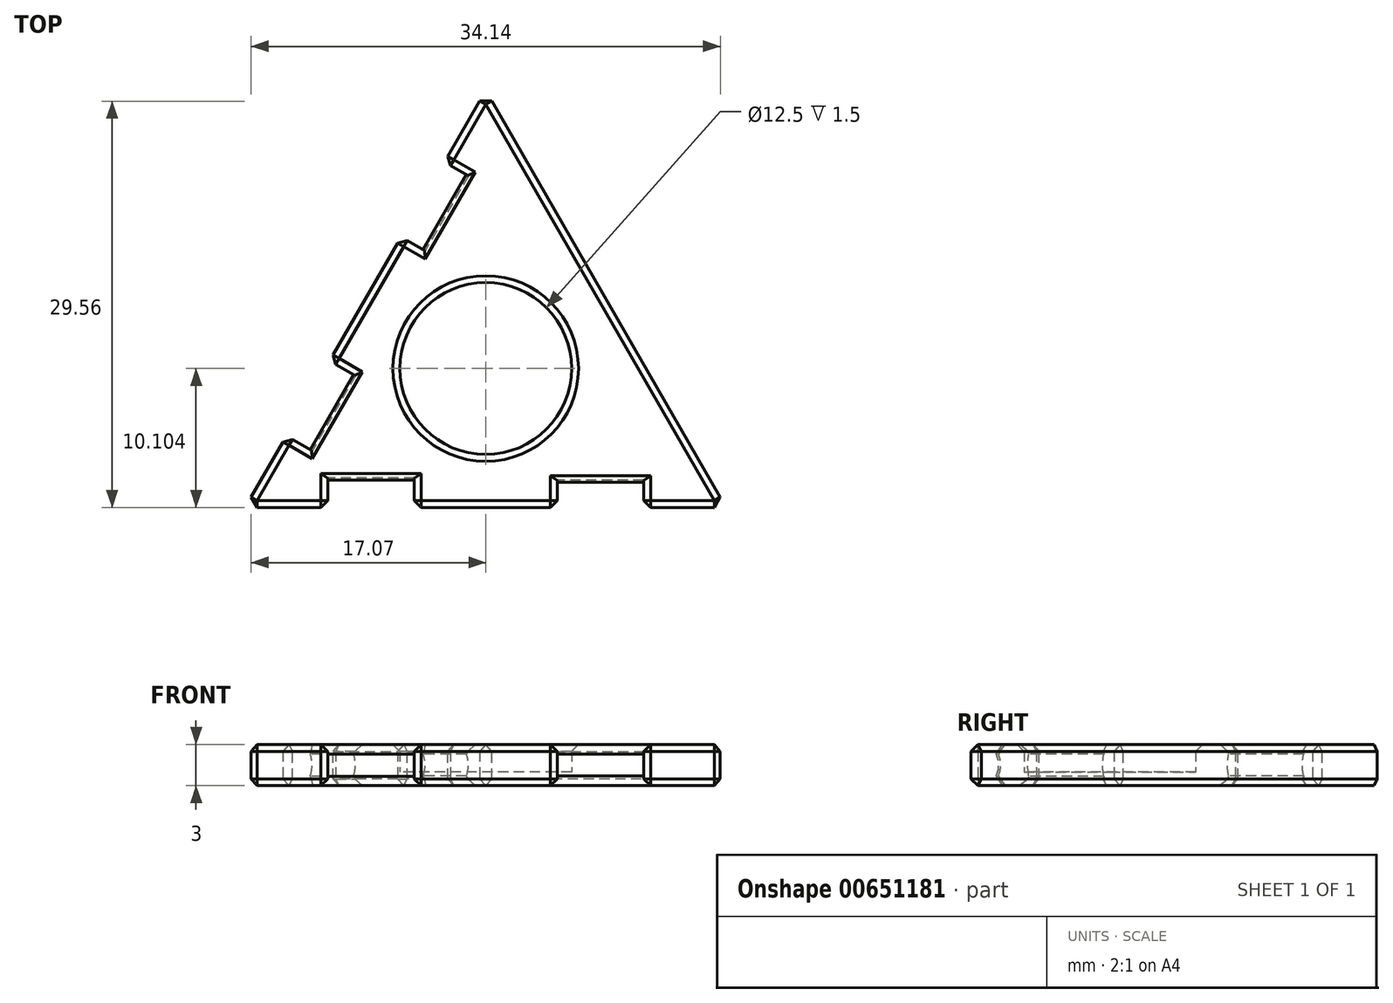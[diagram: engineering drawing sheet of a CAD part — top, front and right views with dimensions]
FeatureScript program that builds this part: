
annotation { "Feature Type Name" : "Feature", "Feature Type Description" : "" }
export const myFeature = defineFeature(function(context is Context, id is Id, definition is map)
    precondition{}
    {
        {
            var Q0;
            Q0=qCreatedBy(makeId("Top.planeOp"),FACE);
            cPlane(context, id + "F0", {"entities" : qUnion([Q0]), "cplaneType" : CPlaneType.OFFSET, "offset" : 1.5 * mm, "oppositeDirection" : true, "width" : 150 * mm, "height" : 150 * mm});
        }
        {
            var Q0;
            Q0=qCreatedBy(id+"F0.planeOp",FACE);
            var sketch = newSketch(context, id + "F1", { "sketchPlane" : qUnion([Q0])});
            skLineSegment(sketch, "E0", {"start": v(-17.5, 0) * mm, "end": v(0, 30.31) * mm});
            skLineSegment(sketch, "E1", {"start": v(0, 30.31) * mm, "end": v(17.5, 0) * mm});
            skLineSegment(sketch, "E2", {"start": v(17.5, 0) * mm, "end": v(-17.5, 0) * mm});
            skLineSegment(sketch, "E3", {"start": v(0, 0) * mm, "end": v(0, 30.31) * mm, "construction": true});
            skCircle(sketch, "E4", {"center": v(0, 10.1) * mm, "radius": 6.25 * mm});
            skLineSegment(sketch, "E5", {"start": v(-17.5, 0) * mm, "end": v(8.75, 15.16) * mm, "construction": true});
            skLineSegment(sketch, "E6", {"start": v(17.5, 0) * mm, "end": v(-8.75, 15.16) * mm, "construction": true});
            skSolve(sketch);
        }
        {
            var Q0;
            Q0 = qSketchRegion(id + "F1", true);
            var Q1;
            Q1=makeQuery(id+"F1.imprint","IMPRINT",FACE,{"disambiguationData":[TD([[makeQuery(id+"F1.imprint","IMPRINT",EDGE,{"derivedFrom":sQuery(id+"F1.wireOp",EDGE,"E4")}),1.0]])]});
            extrude(context, id + "F2", {"entities" : qUnion([Q0, Q1]), "depth" : 1 * mm, "offsetDistance" : 25 * mm});
        }
        {
            var Q0;
            Q0 = qSketchRegion(id + "F1", true);
            extrude(context, id + "F3", {"entities" : qUnion([Q0]), "operationType" : NewBodyOperationType.ADD, "depth" : 3 * mm, "offsetDistance" : 25 * mm});
        }
        {
            var Q0;
            Q0=qCreatedBy(makeId("Top.planeOp"),FACE);
            var sketch = newSketch(context, id + "F4", { "sketchPlane" : qUnion([Q0])});
            skLineSegment(sketch, "E7.bottom", {"start": v(-3, 25.11) * mm, "end": v(-4.73, 26.11) * mm});
            skLineSegment(sketch, "E7.top", {"start": v(-6.15, 19.66) * mm, "end": v(-7.88, 20.66) * mm});
            skLineSegment(sketch, "E7.right", {"start": v(-4.73, 26.11) * mm, "end": v(-7.88, 20.66) * mm});
            skLineSegment(sketch, "E8.bottom", {"start": v(-11.35, 10.65) * mm, "end": v(-13.21, 11.73) * mm});
            skLineSegment(sketch, "E8.top", {"start": v(-14.5, 5.2) * mm, "end": v(-16.36, 6.27) * mm});
            skLineSegment(sketch, "E8.right", {"start": v(-13.21, 11.73) * mm, "end": v(-16.36, 6.27) * mm});
            skLineSegment(sketch, "E9", {"start": v(-3, 25.11) * mm, "end": v(-6.15, 19.66) * mm});
            skLineSegment(sketch, "E10", {"start": v(-11.35, 10.65) * mm, "end": v(-14.5, 5.2) * mm});
            skPoint(sketch, "E8.left.start.orphan", {"position": v(-9.49, 9.58) * mm});
            skPoint(sketch, "E11.orphan", {"position": v(-12.64, 4.12) * mm});
            skPoint(sketch, "E7.left.end.orphan", {"position": v(-4.42, 18.66) * mm});
            skPoint(sketch, "E12.orphan", {"position": v(-1.27, 24.11) * mm});
            skLineSegment(sketch, "E13.MirrorCS", {"start": v(-5.2, -2.15) * mm, "end": v(-11.5, -2.15) * mm});
            skLineSegment(sketch, "E14.MirrorCS", {"start": v(-11.5, 0) * mm, "end": v(-11.5, -2.15) * mm});
            skLineSegment(sketch, "E15.MirrorCS", {"start": v(-5.2, 0) * mm, "end": v(-11.5, 0) * mm});
            skLineSegment(sketch, "E16.MirrorCS", {"start": v(-5.2, 0) * mm, "end": v(-5.2, -2.15) * mm});
            skLineSegment(sketch, "E17.MirrorCS", {"start": v(5.2, 0) * mm, "end": v(5.2, -2) * mm});
            skLineSegment(sketch, "E18.MirrorCS", {"start": v(11.5, -2) * mm, "end": v(5.2, -2) * mm});
            skLineSegment(sketch, "E19.MirrorCS", {"start": v(11.5, 0) * mm, "end": v(5.2, 0) * mm});
            skLineSegment(sketch, "E20.MirrorCS", {"start": v(11.5, 0) * mm, "end": v(11.5, -2) * mm});
            skSolve(sketch);
        }
        {
            var Q0;
            Q0=makeQuery(id+"F4.imprint","IMPRINT",FACE,{"disambiguationData":[TD([[makeQuery(id+"F4.imprint","IMPRINT",EDGE,{"derivedFrom":sQuery(id+"F4.wireOp",EDGE,"E8.bottom")}),1.0]])]});
            var Q1;
            Q1=makeQuery(id+"F4.imprint","IMPRINT",FACE,{"disambiguationData":[TD([[makeQuery(id+"F4.imprint","IMPRINT",EDGE,{"derivedFrom":sQuery(id+"F4.wireOp",EDGE,"E7.bottom")}),1.0]])]});
            var Q2;
            Q2=sQuery(id+"F4.wireOp",EDGE,"E10");
            revolve(context, id + "F5", {"operationType" : NewBodyOperationType.REMOVE, "entities" : qUnion([Q0, Q1]), "axis" : qUnion([Q2]), "revolveType" : RevolveType.FULL, "oppositeDirection" : true});
        }
        {
            var Q0;
            Q0=makeQuery(id+"F4.imprint","IMPRINT",FACE,{"disambiguationData":[TD([[makeQuery(id+"F4.imprint","IMPRINT",EDGE,{"derivedFrom":sQuery(id+"F4.wireOp",EDGE,"E13.MirrorCS")}),-1.0]])]});
            var Q1;
            Q1=makeQuery(id+"F4.imprint","IMPRINT",FACE,{"disambiguationData":[TD([[makeQuery(id+"F4.imprint","IMPRINT",EDGE,{"derivedFrom":sQuery(id+"F4.wireOp",EDGE,"E17.MirrorCS")}),1.0]])]});
            var Q2;
            Q2=sQuery(id+"F4.wireOp",EDGE,"E15.MirrorCS");
            revolve(context, id + "F6", {"operationType" : NewBodyOperationType.REMOVE, "entities" : qUnion([Q0, Q1]), "axis" : qUnion([Q2]), "revolveType" : RevolveType.FULL, "oppositeDirection" : true});
        }
        {
            var Q0;
            Q0=makeQuery(id+"F3.opExtrude","CAP_FACE",FACE,{"disambiguationData":[OSD([sQuery(id+"F1.wireOp",EDGE,"E0"),sQuery(id+"F1.wireOp",EDGE,"E1"),sQuery(id+"F1.wireOp",EDGE,"E2"),sQuery(id+"F1.wireOp",EDGE,"E4")])],"isStart":false});
            var Q1;
            Q1=makeQuery(id+"F2.opExtrude","CAP_FACE",FACE,{"disambiguationData":[OSD([sQuery(id+"F1.wireOp",EDGE,"E0"),sQuery(id+"F1.wireOp",EDGE,"E1"),sQuery(id+"F1.wireOp",EDGE,"E2")])],"isStart":true});
            var Q2;
            {var subQ0=sQuery(id+"F1.wireOp",EDGE,"E2");Q2=makeQuery(id+"F6.boolean.opBoolean","INTERSECT",EDGE,{"derivedFrom":[makeQuery(id+"F3.boolean.opBoolean","MERGE",FACE,{"derivedFrom":[makeQuery(id+"F2.opExtrude","SWEPT_FACE",FACE,{"disambiguationData":[OSD([subQ0])]}),makeQuery(id+"F3.opExtrude","SWEPT_FACE",FACE,{"disambiguationData":[OSD([subQ0])]})]}),makeQuery(id+"F6.opRevolve","SWEPT_FACE",FACE,{"disambiguationData":[OSD([sQuery(id+"F4.wireOp",EDGE,"E17.MirrorCS")])]})]});}
            var Q3;
            {var subQ0=sQuery(id+"F1.wireOp",EDGE,"E2");Q3=makeQuery(id+"F6.boolean.opBoolean","INTERSECT",EDGE,{"derivedFrom":[makeQuery(id+"F3.boolean.opBoolean","MERGE",FACE,{"derivedFrom":[makeQuery(id+"F2.opExtrude","SWEPT_FACE",FACE,{"disambiguationData":[OSD([subQ0])]}),makeQuery(id+"F3.opExtrude","SWEPT_FACE",FACE,{"disambiguationData":[OSD([subQ0])]})]}),makeQuery(id+"F6.opRevolve","SWEPT_FACE",FACE,{"disambiguationData":[OSD([sQuery(id+"F4.wireOp",EDGE,"E20.MirrorCS")])]})]});}
            var Q4;
            {var subQ0=sQuery(id+"F1.wireOp",EDGE,"E2");Q4=makeQuery(id+"F6.boolean.opBoolean","INTERSECT",EDGE,{"derivedFrom":[makeQuery(id+"F3.boolean.opBoolean","MERGE",FACE,{"derivedFrom":[makeQuery(id+"F2.opExtrude","SWEPT_FACE",FACE,{"disambiguationData":[OSD([subQ0])]}),makeQuery(id+"F3.opExtrude","SWEPT_FACE",FACE,{"disambiguationData":[OSD([subQ0])]})]}),makeQuery(id+"F6.opRevolve","SWEPT_FACE",FACE,{"disambiguationData":[OSD([sQuery(id+"F4.wireOp",EDGE,"E14.MirrorCS")])]})]});}
            var Q5;
            {var subQ0=sQuery(id+"F1.wireOp",EDGE,"E2");Q5=makeQuery(id+"F6.boolean.opBoolean","INTERSECT",EDGE,{"derivedFrom":[makeQuery(id+"F3.boolean.opBoolean","MERGE",FACE,{"derivedFrom":[makeQuery(id+"F2.opExtrude","SWEPT_FACE",FACE,{"disambiguationData":[OSD([subQ0])]}),makeQuery(id+"F3.opExtrude","SWEPT_FACE",FACE,{"disambiguationData":[OSD([subQ0])]})]}),makeQuery(id+"F6.opRevolve","SWEPT_FACE",FACE,{"disambiguationData":[OSD([sQuery(id+"F4.wireOp",EDGE,"E16.MirrorCS")])]})]});}
            var Q6;
            {var subQ0=sQuery(id+"F1.wireOp",EDGE,"E1");Q6=makeQuery(id+"Flts4oeSLqaGHYI_1.1.F5.boolean.opBoolean","INTERSECT",EDGE,{"derivedFrom":[makeQuery(id+"F3.boolean.opBoolean","MERGE",FACE,{"derivedFrom":[makeQuery(id+"F2.opExtrude","SWEPT_FACE",FACE,{"disambiguationData":[OSD([subQ0])]}),makeQuery(id+"F3.opExtrude","SWEPT_FACE",FACE,{"disambiguationData":[OSD([subQ0])]})]}),makeQuery(id+"Flts4oeSLqaGHYI_1.1.F5.opRevolve","SWEPT_FACE",FACE,{"disambiguationData":[OSD([sQuery(id+"F4.wireOp",EDGE,"E8.top")])]})]});}
            var Q7;
            {var subQ0=sQuery(id+"F1.wireOp",EDGE,"E1");Q7=makeQuery(id+"Flts4oeSLqaGHYI_1.1.F5.boolean.opBoolean","INTERSECT",EDGE,{"derivedFrom":[makeQuery(id+"F3.boolean.opBoolean","MERGE",FACE,{"derivedFrom":[makeQuery(id+"F2.opExtrude","SWEPT_FACE",FACE,{"disambiguationData":[OSD([subQ0])]}),makeQuery(id+"F3.opExtrude","SWEPT_FACE",FACE,{"disambiguationData":[OSD([subQ0])]})]}),makeQuery(id+"Flts4oeSLqaGHYI_1.1.F5.opRevolve","SWEPT_FACE",FACE,{"disambiguationData":[OSD([sQuery(id+"F4.wireOp",EDGE,"E8.bottom")])]})]});}
            var Q8;
            {var subQ0=sQuery(id+"F1.wireOp",EDGE,"E1");Q8=makeQuery(id+"Flts4oeSLqaGHYI_1.1.F5.boolean.opBoolean","INTERSECT",EDGE,{"derivedFrom":[makeQuery(id+"F3.boolean.opBoolean","MERGE",FACE,{"derivedFrom":[makeQuery(id+"F2.opExtrude","SWEPT_FACE",FACE,{"disambiguationData":[OSD([subQ0])]}),makeQuery(id+"F3.opExtrude","SWEPT_FACE",FACE,{"disambiguationData":[OSD([subQ0])]})]}),makeQuery(id+"Flts4oeSLqaGHYI_1.1.F5.opRevolve","SWEPT_FACE",FACE,{"disambiguationData":[OSD([sQuery(id+"F4.wireOp",EDGE,"E7.top")])]})]});}
            var Q9;
            {var subQ0=sQuery(id+"F1.wireOp",EDGE,"E1");Q9=makeQuery(id+"Flts4oeSLqaGHYI_1.1.F5.boolean.opBoolean","INTERSECT",EDGE,{"derivedFrom":[makeQuery(id+"F3.boolean.opBoolean","MERGE",FACE,{"derivedFrom":[makeQuery(id+"F2.opExtrude","SWEPT_FACE",FACE,{"disambiguationData":[OSD([subQ0])]}),makeQuery(id+"F3.opExtrude","SWEPT_FACE",FACE,{"disambiguationData":[OSD([subQ0])]})]}),makeQuery(id+"Flts4oeSLqaGHYI_1.1.F5.opRevolve","SWEPT_FACE",FACE,{"disambiguationData":[OSD([sQuery(id+"F4.wireOp",EDGE,"E7.bottom")])]})]});}
            var Q10;
            {var subQ0=sQuery(id+"F1.wireOp",EDGE,"E1");var subQ1=sQuery(id+"F1.wireOp",EDGE,"E0");Q10=makeQuery(id+"F3.boolean.opBoolean","MERGE",EDGE,{"derivedFrom":[makeQuery(id+"F2.opExtrude","SWEPT_EDGE",EDGE,{"disambiguationData":[OSD([subQ1,subQ0])]}),makeQuery(id+"F3.opExtrude","SWEPT_EDGE",EDGE,{"disambiguationData":[OSD([subQ1,subQ0])]})]});}
            var Q11;
            {var subQ0=sQuery(id+"F1.wireOp",EDGE,"E2");var subQ1=sQuery(id+"F1.wireOp",EDGE,"E1");Q11=makeQuery(id+"F3.boolean.opBoolean","MERGE",EDGE,{"derivedFrom":[makeQuery(id+"F2.opExtrude","SWEPT_EDGE",EDGE,{"disambiguationData":[OSD([subQ1,subQ0])]}),makeQuery(id+"F3.opExtrude","SWEPT_EDGE",EDGE,{"disambiguationData":[OSD([subQ1,subQ0])]})]});}
            var Q12;
            {var subQ0=sQuery(id+"F1.wireOp",EDGE,"E0");Q12=makeQuery(id+"F5.boolean.opBoolean","INTERSECT",EDGE,{"derivedFrom":[makeQuery(id+"F3.boolean.opBoolean","MERGE",FACE,{"derivedFrom":[makeQuery(id+"F2.opExtrude","SWEPT_FACE",FACE,{"disambiguationData":[OSD([subQ0])]}),makeQuery(id+"F3.opExtrude","SWEPT_FACE",FACE,{"disambiguationData":[OSD([subQ0])]})]}),makeQuery(id+"F5.opRevolve","SWEPT_FACE",FACE,{"disambiguationData":[OSD([sQuery(id+"F4.wireOp",EDGE,"E7.bottom")])]})]});}
            var Q13;
            {var subQ0=sQuery(id+"F1.wireOp",EDGE,"E0");Q13=makeQuery(id+"F5.boolean.opBoolean","INTERSECT",EDGE,{"derivedFrom":[makeQuery(id+"F3.boolean.opBoolean","MERGE",FACE,{"derivedFrom":[makeQuery(id+"F2.opExtrude","SWEPT_FACE",FACE,{"disambiguationData":[OSD([subQ0])]}),makeQuery(id+"F3.opExtrude","SWEPT_FACE",FACE,{"disambiguationData":[OSD([subQ0])]})]}),makeQuery(id+"F5.opRevolve","SWEPT_FACE",FACE,{"disambiguationData":[OSD([sQuery(id+"F4.wireOp",EDGE,"E7.top")])]})]});}
            var Q14;
            {var subQ0=sQuery(id+"F1.wireOp",EDGE,"E0");Q14=makeQuery(id+"F5.boolean.opBoolean","INTERSECT",EDGE,{"derivedFrom":[makeQuery(id+"F3.boolean.opBoolean","MERGE",FACE,{"derivedFrom":[makeQuery(id+"F2.opExtrude","SWEPT_FACE",FACE,{"disambiguationData":[OSD([subQ0])]}),makeQuery(id+"F3.opExtrude","SWEPT_FACE",FACE,{"disambiguationData":[OSD([subQ0])]})]}),makeQuery(id+"F5.opRevolve","SWEPT_FACE",FACE,{"disambiguationData":[OSD([sQuery(id+"F4.wireOp",EDGE,"E8.bottom")])]})]});}
            var Q15;
            {var subQ0=sQuery(id+"F1.wireOp",EDGE,"E0");Q15=makeQuery(id+"F5.boolean.opBoolean","INTERSECT",EDGE,{"derivedFrom":[makeQuery(id+"F3.boolean.opBoolean","MERGE",FACE,{"derivedFrom":[makeQuery(id+"F2.opExtrude","SWEPT_FACE",FACE,{"disambiguationData":[OSD([subQ0])]}),makeQuery(id+"F3.opExtrude","SWEPT_FACE",FACE,{"disambiguationData":[OSD([subQ0])]})]}),makeQuery(id+"F5.opRevolve","SWEPT_FACE",FACE,{"disambiguationData":[OSD([sQuery(id+"F4.wireOp",EDGE,"E8.top")])]})]});}
            var Q16;
            {var subQ0=sQuery(id+"F1.wireOp",EDGE,"E2");var subQ1=sQuery(id+"F1.wireOp",EDGE,"E0");Q16=makeQuery(id+"F3.boolean.opBoolean","MERGE",EDGE,{"derivedFrom":[makeQuery(id+"F2.opExtrude","SWEPT_EDGE",EDGE,{"disambiguationData":[OSD([subQ1,subQ0])]}),makeQuery(id+"F3.opExtrude","SWEPT_EDGE",EDGE,{"disambiguationData":[OSD([subQ1,subQ0])]})]});}
            chamfer(context, id + "F7", {"entities" : qUnion([Q0, Q1, Q2, Q3, Q4, Q5, Q6, Q7, Q8, Q9, Q10, Q11, Q12, Q13, Q14, Q15, Q16]), "width" : 0.5 * mm, "tangentPropagation" : true});
        }
    });
